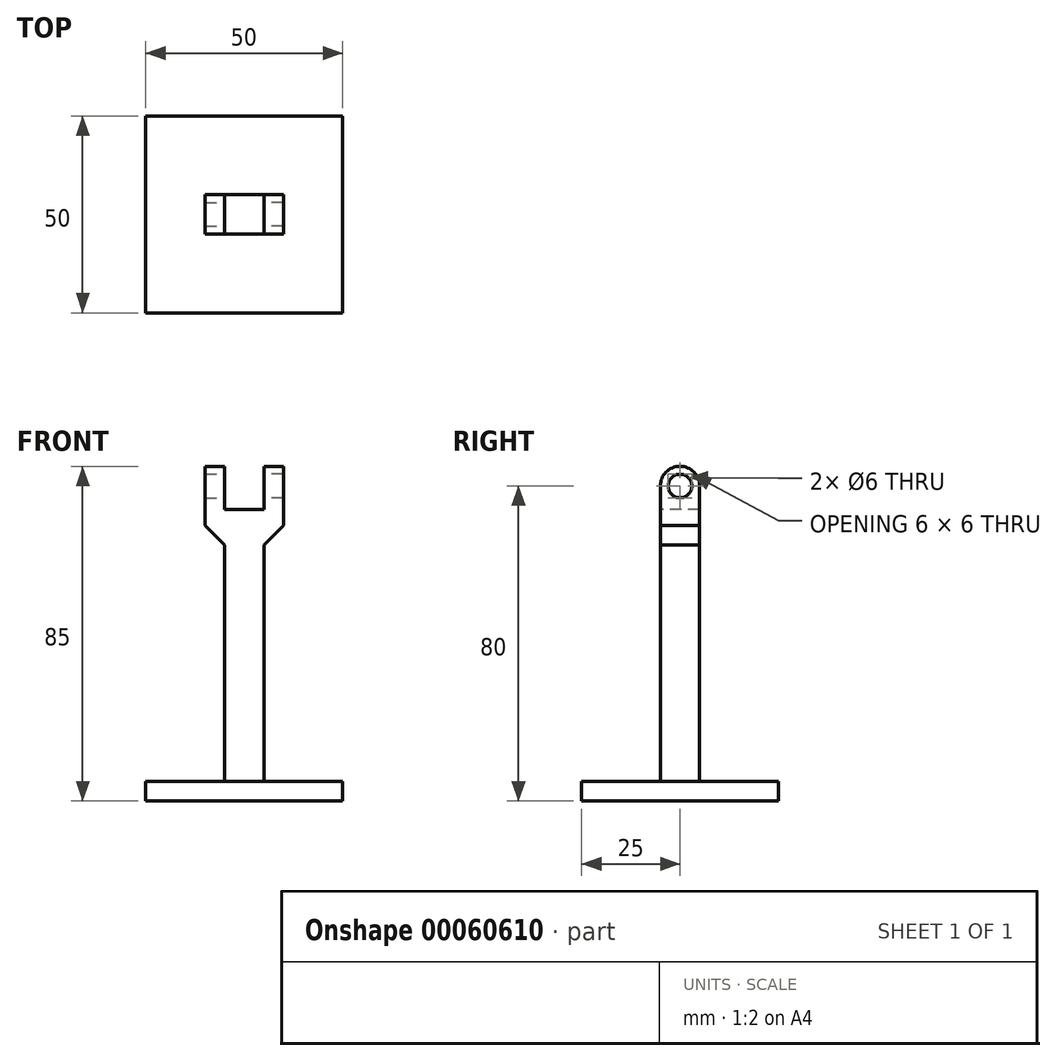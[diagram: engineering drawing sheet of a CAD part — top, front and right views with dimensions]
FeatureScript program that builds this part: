
annotation { "Feature Type Name" : "Feature", "Feature Type Description" : "" }
export const myFeature = defineFeature(function(context is Context, id is Id, definition is map)
    precondition{}
    {
        {
            var Q0;
            Q0=qCreatedBy(makeId("Top.planeOp"),FACE);
            var sketch = newSketch(context, id + "F0", { "sketchPlane" : qUnion([Q0])});
            skLineSegment(sketch, "E0.rect.bottom", {"start": v(-25, 25) * mm, "end": v(25, 25) * mm});
            skLineSegment(sketch, "E0.rect.top", {"start": v(-25, -25) * mm, "end": v(25, -25) * mm});
            skLineSegment(sketch, "E0.rect.left", {"start": v(-25, 25) * mm, "end": v(-25, -25) * mm});
            skLineSegment(sketch, "E0.rect.right", {"start": v(25, 25) * mm, "end": v(25, -25) * mm});
            skPoint(sketch, "E0.rect.middle", {"position": v(0, 0) * mm});
            skLineSegment(sketch, "E1.rect.bottom", {"start": v(-5, 5) * mm, "end": v(5, 5) * mm});
            skLineSegment(sketch, "E1.rect.top", {"start": v(-5, -5) * mm, "end": v(5, -5) * mm});
            skLineSegment(sketch, "E1.rect.left", {"start": v(-5, 5) * mm, "end": v(-5, -5) * mm});
            skLineSegment(sketch, "E1.rect.right", {"start": v(5, 5) * mm, "end": v(5, -5) * mm});
            skSolve(sketch);
        }
        {
            var Q0;
            Q0=makeQuery(id+"F0.imprint","IMPRINT",FACE,{"disambiguationData":[TD([[makeQuery(id+"F0.imprint","IMPRINT",EDGE,{"derivedFrom":sQuery(id+"F0.wireOp",EDGE,"E0.rect.bottom")}),-1.0]])]});
            extrude(context, id + "F1", {"entities" : qUnion([Q0]), "depth" : 5 * mm});
        }
        {
            var Q0;
            Q0=makeQuery(id+"F0.imprint","IMPRINT",FACE,{"disambiguationData":[TD([[makeQuery(id+"F0.imprint","IMPRINT",EDGE,{"derivedFrom":sQuery(id+"F0.wireOp",EDGE,"E1.rect.bottom")}),-1.0]])]});
            extrude(context, id + "F2", {"entities" : qUnion([Q0]), "operationType" : NewBodyOperationType.ADD, "depth" : 75 * mm});
        }
        {
            var Q0;
            Q0=makeQuery(id+"F2.opExtrude","SWEPT_FACE",FACE,{"disambiguationData":[OSD([sQuery(id+"F0.wireOp",EDGE,"E1.rect.right")])]});
            var sketch = newSketch(context, id + "F3", { "sketchPlane" : qUnion([Q0])});
            skLineSegment(sketch, "E2.bottom", {"start": v(5, 75) * mm, "end": v(-5, 75) * mm});
            skLineSegment(sketch, "E2.top", {"start": v(5, 70) * mm, "end": v(-5, 70) * mm});
            skLineSegment(sketch, "E2.left", {"start": v(5, 75) * mm, "end": v(5, 70) * mm});
            skLineSegment(sketch, "E2.right", {"start": v(-5, 75) * mm, "end": v(-5, 70) * mm});
            skSolve(sketch);
        }
        {
            var Q0;
            Q0=makeQuery(id+"F3.imprint","IMPRINT",FACE,{"disambiguationData":[TD([[makeQuery(id+"F3.imprint","IMPRINT",EDGE,{"derivedFrom":sQuery(id+"F3.wireOp",EDGE,"E2.bottom")}),1.0]])]});
            extrude(context, id + "F4", {"entities" : qUnion([Q0]), "operationType" : NewBodyOperationType.ADD, "depth" : 5 * mm});
        }
        {
            var Q0;
            Q0=makeQuery(id+"F2.opExtrude","SWEPT_FACE",FACE,{"disambiguationData":[OSD([sQuery(id+"F0.wireOp",EDGE,"E1.rect.left")])]});
            var sketch = newSketch(context, id + "F5", { "sketchPlane" : qUnion([Q0])});
            skLineSegment(sketch, "E3.bottom", {"start": v(5, 75) * mm, "end": v(-5, 75) * mm});
            skLineSegment(sketch, "E3.top", {"start": v(5, 70) * mm, "end": v(-5, 70) * mm});
            skLineSegment(sketch, "E3.left", {"start": v(5, 75) * mm, "end": v(5, 70) * mm});
            skLineSegment(sketch, "E3.right", {"start": v(-5, 75) * mm, "end": v(-5, 70) * mm});
            skSolve(sketch);
        }
        {
            var Q0;
            Q0=makeQuery(id+"F5.imprint","IMPRINT",FACE,{"disambiguationData":[TD([[makeQuery(id+"F5.imprint","IMPRINT",EDGE,{"derivedFrom":sQuery(id+"F5.wireOp",EDGE,"E3.bottom")}),-1.0]])]});
            extrude(context, id + "F6", {"entities" : qUnion([Q0]), "operationType" : NewBodyOperationType.ADD, "depth" : 5 * mm});
        }
        {
            var Q0;
            Q0=makeQuery(id+"F6.boolean.opBoolean","MERGE",FACE,{"derivedFrom":[makeQuery(id+"F4.boolean.opBoolean","MERGE",FACE,{"derivedFrom":[makeQuery(id+"F2.opExtrude","CAP_FACE",FACE,{"disambiguationData":[OSD([sQuery(id+"F0.wireOp",EDGE,"E1.rect.bottom"),sQuery(id+"F0.wireOp",EDGE,"E1.rect.top"),sQuery(id+"F0.wireOp",EDGE,"E1.rect.left"),sQuery(id+"F0.wireOp",EDGE,"E1.rect.right")])],"isStart":false}),makeQuery(id+"F4.opExtrude","SWEPT_FACE",FACE,{"disambiguationData":[OSD([sQuery(id+"F3.wireOp",EDGE,"E2.bottom")])]})]}),makeQuery(id+"F6.opExtrude","SWEPT_FACE",FACE,{"disambiguationData":[OSD([sQuery(id+"F5.wireOp",EDGE,"E3.bottom")])]})]});
            var sketch = newSketch(context, id + "F7", { "sketchPlane" : qUnion([Q0])});
            skLineSegment(sketch, "E4.bottom", {"start": v(10, 5) * mm, "end": v(5, 5) * mm});
            skLineSegment(sketch, "E4.top", {"start": v(10, -5) * mm, "end": v(5, -5) * mm});
            skLineSegment(sketch, "E4.left", {"start": v(10, 5) * mm, "end": v(10, -5) * mm});
            skLineSegment(sketch, "E4.right", {"start": v(5, 5) * mm, "end": v(5, -5) * mm});
            skLineSegment(sketch, "E5.bottom", {"start": v(-10, -5) * mm, "end": v(-5, -5) * mm});
            skLineSegment(sketch, "E5.top", {"start": v(-10, 5) * mm, "end": v(-5, 5) * mm});
            skLineSegment(sketch, "E5.left", {"start": v(-10, -5) * mm, "end": v(-10, 5) * mm});
            skLineSegment(sketch, "E5.right", {"start": v(-5, -5) * mm, "end": v(-5, 5) * mm});
            skSolve(sketch);
        }
        {
            var Q0;
            Q0=makeQuery(id+"F7.imprint","IMPRINT",FACE,{"disambiguationData":[TD([[makeQuery(id+"F7.imprint","IMPRINT",EDGE,{"derivedFrom":sQuery(id+"F7.wireOp",EDGE,"E4.bottom")}),-1.0]])]});
            var Q1;
            Q1=makeQuery(id+"F7.imprint","IMPRINT",FACE,{"disambiguationData":[TD([[makeQuery(id+"F7.imprint","IMPRINT",EDGE,{"derivedFrom":sQuery(id+"F7.wireOp",EDGE,"E5.bottom")}),1.0]])]});
            extrude(context, id + "F8", {"entities" : qUnion([Q0, Q1]), "operationType" : NewBodyOperationType.ADD, "depth" : 10 * mm});
        }
        {
            var Q0;
            Q0=makeQuery(id+"F8.opExtrude","SWEPT_FACE",FACE,{"disambiguationData":[OSD([sQuery(id+"F7.wireOp",EDGE,"E4.right")])]});
            var sketch = newSketch(context, id + "F9", { "sketchPlane" : qUnion([Q0])});
            skCircle(sketch, "E6", {"center": v(0, 80) * mm, "radius": 3 * mm});
            skSolve(sketch);
        }
        {
            var Q0;
            Q0=sQuery(id+"F9.wireOp",VERTEX,"E6.center");
            var Q1;
            Q1=makeQuery(id+"F1.opExtrude","SWEPT_BODY",BODY,{"disambiguationData":[OSD([sQuery(id+"F0.wireOp",EDGE,"E0.rect.bottom"),sQuery(id+"F0.wireOp",EDGE,"E0.rect.top"),sQuery(id+"F0.wireOp",EDGE,"E0.rect.left"),sQuery(id+"F0.wireOp",EDGE,"E0.rect.right"),sQuery(id+"F0.wireOp",EDGE,"E1.rect.bottom"),sQuery(id+"F0.wireOp",EDGE,"E1.rect.top"),sQuery(id+"F0.wireOp",EDGE,"E1.rect.left"),sQuery(id+"F0.wireOp",EDGE,"E1.rect.right")])]});
            hole(context, id + "F10", {"style" : HoleStyle.SIMPLE, "holeDiameter" : 6 * mm, "endStyle" : HoleEndStyle.THROUGH, "locations" : qUnion([Q0]), "scope" : qUnion([Q1])});
        }
        {
            var Q0;
            Q0=makeQuery(id+"F8.opExtrude","SWEPT_FACE",FACE,{"disambiguationData":[OSD([sQuery(id+"F7.wireOp",EDGE,"E5.right")])]});
            var sketch = newSketch(context, id + "F11", { "sketchPlane" : qUnion([Q0])});
            skCircle(sketch, "E7", {"center": v(0, 80) * mm, "radius": 3 * mm});
            skSolve(sketch);
        }
        {
            var Q0;
            Q0=sQuery(id+"F11.wireOp",VERTEX,"E7.center");
            var Q1;
            Q1=makeQuery(id+"F1.opExtrude","SWEPT_BODY",BODY,{"disambiguationData":[OSD([sQuery(id+"F0.wireOp",EDGE,"E0.rect.bottom"),sQuery(id+"F0.wireOp",EDGE,"E0.rect.top"),sQuery(id+"F0.wireOp",EDGE,"E0.rect.left"),sQuery(id+"F0.wireOp",EDGE,"E0.rect.right"),sQuery(id+"F0.wireOp",EDGE,"E1.rect.bottom"),sQuery(id+"F0.wireOp",EDGE,"E1.rect.top"),sQuery(id+"F0.wireOp",EDGE,"E1.rect.left"),sQuery(id+"F0.wireOp",EDGE,"E1.rect.right")])]});
            hole(context, id + "F12", {"style" : HoleStyle.SIMPLE, "holeDiameter" : 6 * mm, "endStyle" : HoleEndStyle.THROUGH, "locations" : qUnion([Q0]), "scope" : qUnion([Q1])});
        }
        {
            var Q0;
            Q0=makeQuery(id+"F8.opExtrude","CAP_EDGE",EDGE,{"disambiguationData":[OSD([sQuery(id+"F7.wireOp",EDGE,"E5.bottom")])],"isStart":false});
            var Q1;
            Q1=makeQuery(id+"F8.opExtrude","CAP_EDGE",EDGE,{"disambiguationData":[OSD([sQuery(id+"F7.wireOp",EDGE,"E4.top")])],"isStart":false});
            var Q2;
            Q2=makeQuery(id+"F8.opExtrude","CAP_EDGE",EDGE,{"disambiguationData":[OSD([sQuery(id+"F7.wireOp",EDGE,"E4.bottom")])],"isStart":false});
            var Q3;
            Q3=makeQuery(id+"F8.opExtrude","CAP_EDGE",EDGE,{"disambiguationData":[OSD([sQuery(id+"F7.wireOp",EDGE,"E5.top")])],"isStart":false});
            fillet(context, id + "F13", {"entities" : qUnion([Q0, Q1, Q2, Q3]), "radius" : 5 * mm, "tangentPropagation" : true, "allowEdgeOverflow" : false});
        }
        {
            var Q0;
            Q0=makeQuery(id+"F6.boolean.opBoolean","MERGE",FACE,{"derivedFrom":[makeQuery(id+"F4.boolean.opBoolean","MERGE",FACE,{"derivedFrom":[makeQuery(id+"F2.opExtrude","CAP_FACE",FACE,{"disambiguationData":[OSD([sQuery(id+"F0.wireOp",EDGE,"E1.rect.bottom"),sQuery(id+"F0.wireOp",EDGE,"E1.rect.top"),sQuery(id+"F0.wireOp",EDGE,"E1.rect.left"),sQuery(id+"F0.wireOp",EDGE,"E1.rect.right")])],"isStart":false}),makeQuery(id+"F4.opExtrude","SWEPT_FACE",FACE,{"disambiguationData":[OSD([sQuery(id+"F3.wireOp",EDGE,"E2.bottom")])]})]}),makeQuery(id+"F6.opExtrude","SWEPT_FACE",FACE,{"disambiguationData":[OSD([sQuery(id+"F5.wireOp",EDGE,"E3.bottom")])]})]});
            extrude(context, id + "F14", {"entities" : qUnion([Q0]), "operationType" : NewBodyOperationType.REMOVE, "oppositeDirection" : true, "depth" : 1 * mm});
        }
        {
            var Q0;
            Q0=makeQuery(id+"F4.opExtrude","SWEPT_FACE",FACE,{"disambiguationData":[OSD([sQuery(id+"F3.wireOp",EDGE,"E2.top")])]});
            var Q1;
            Q1=makeQuery(id+"F6.opExtrude","SWEPT_FACE",FACE,{"disambiguationData":[OSD([sQuery(id+"F5.wireOp",EDGE,"E3.top")])]});
            extrude(context, id + "F15", {"entities" : qUnion([Q0, Q1]), "operationType" : NewBodyOperationType.ADD, "depth" : 5 * mm});
        }
        {
            var Q0;
            {var subQ0=sQuery(id+"F3.wireOp",EDGE,"E2.top");Q0=makeQuery(id+"F15.opExtrude","CAP_EDGE",EDGE,{"disambiguationData":[OSD([subQ0]),TDD([makeQuery(id+"F4.opExtrude","CAP_EDGE",EDGE,{"disambiguationData":[OSD([subQ0])],"isStart":false})])],"isStart":false});}
            var Q1;
            {var subQ0=sQuery(id+"F5.wireOp",EDGE,"E3.top");Q1=makeQuery(id+"F15.opExtrude","CAP_EDGE",EDGE,{"disambiguationData":[OSD([subQ0]),TDD([makeQuery(id+"F6.opExtrude","CAP_EDGE",EDGE,{"disambiguationData":[OSD([subQ0])],"isStart":false})])],"isStart":false});}
            chamfer(context, id + "F16", {"entities" : qUnion([Q0, Q1]), "width" : 5 * mm, "tangentPropagation" : true});
        }
    });
